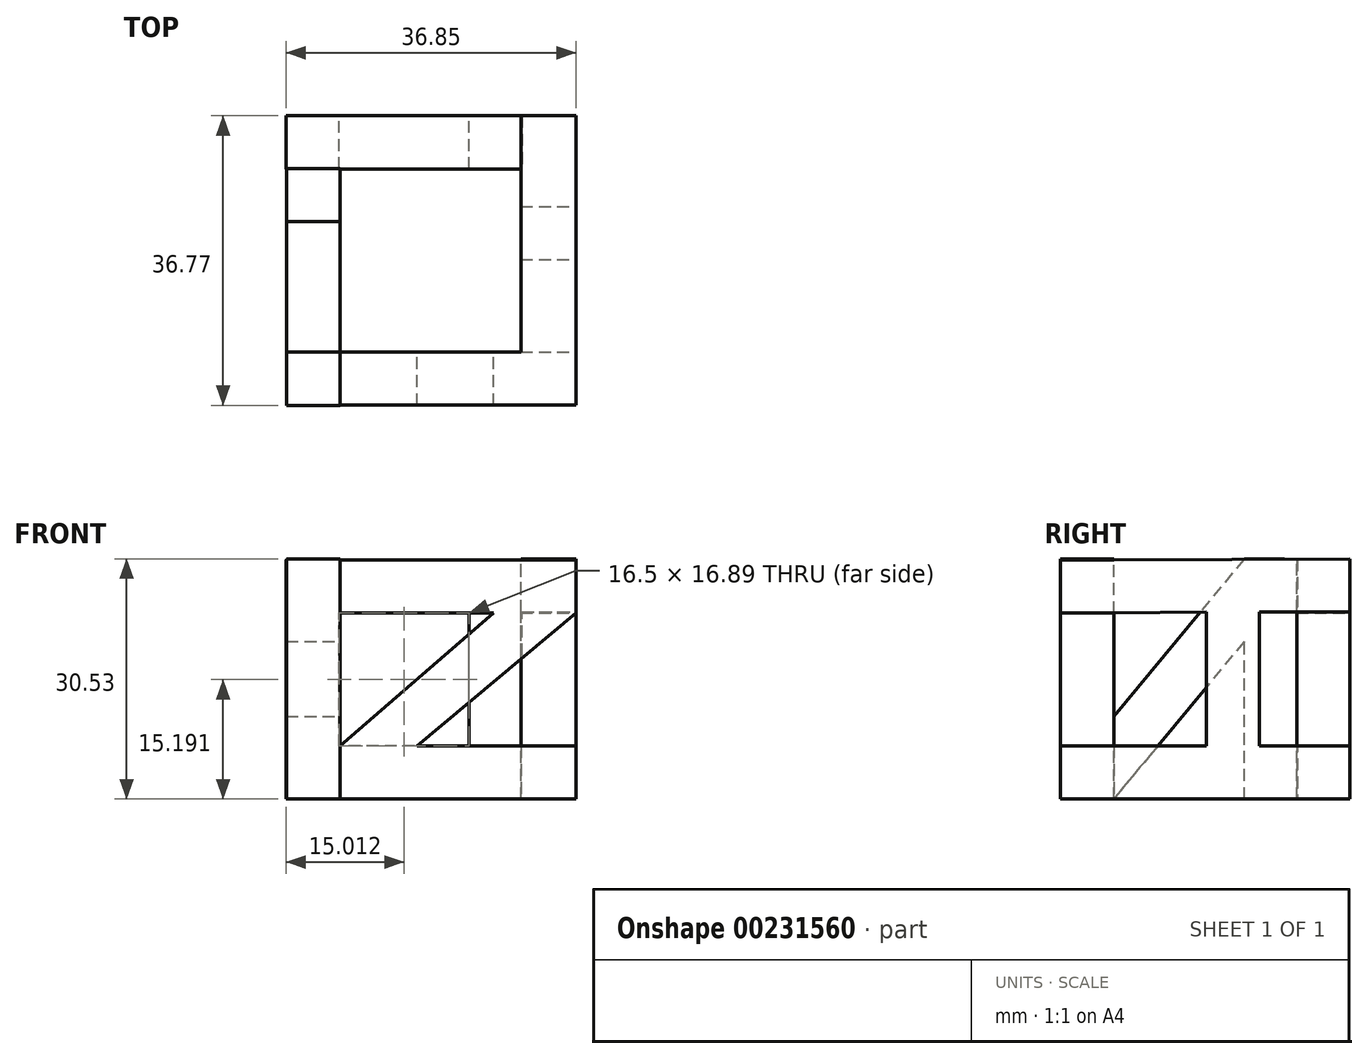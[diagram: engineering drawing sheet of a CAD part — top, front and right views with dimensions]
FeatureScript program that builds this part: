
annotation { "Feature Type Name" : "Feature", "Feature Type Description" : "" }
export const myFeature = defineFeature(function(context is Context, id is Id, definition is map)
    precondition{}
    {
        {
            var Q0;
            Q0=qCreatedBy(makeId("Front.planeOp"),FACE);
            cPlane(context, id + "F0", {"entities" : qUnion([Q0]), "cplaneType" : CPlaneType.OFFSET, "offset" : 30 * mm, "oppositeDirection" : true, "width" : 150 * mm, "height" : 150 * mm});
        }
        {
            var Q0;
            Q0=qCreatedBy(makeId("Front.planeOp"),FACE);
            var sketch = newSketch(context, id + "F1", { "sketchPlane" : qUnion([Q0])});
            skLineSegment(sketch, "E0", {"start": v(-30, -0.01) * mm, "end": v(0, -0.01) * mm});
            skLineSegment(sketch, "E1", {"start": v(0, 30.38) * mm, "end": v(-30, 30.38) * mm});
            skLineSegment(sketch, "E2", {"start": v(-30, 30.38) * mm, "end": v(-30, 23.62) * mm});
            skLineSegment(sketch, "E3", {"start": v(-30, 23.62) * mm, "end": v(-10.5, 23.62) * mm});
            skLineSegment(sketch, "E4", {"start": v(0, 23.62) * mm, "end": v(0, 30.38) * mm});
            skLineSegment(sketch, "E5", {"start": v(-30, -0.01) * mm, "end": v(-30, 6.74) * mm});
            skLineSegment(sketch, "E6", {"start": v(0, 6.74) * mm, "end": v(0, -0.01) * mm});
            skLineSegment(sketch, "E7.trimOffspring", {"start": v(-20.2, 6.74) * mm, "end": v(0, 6.74) * mm});
            skLineSegment(sketch, "E8", {"start": v(-20.2, 6.74) * mm, "end": v(0, 23.62) * mm});
            skLineSegment(sketch, "E9", {"start": v(-30, 6.74) * mm, "end": v(-10.5, 23.62) * mm});
            skSolve(sketch);
        }
        {
            var Q0;
            Q0=qCreatedBy(makeId("Right.planeOp"),FACE);
            var sketch = newSketch(context, id + "F2", { "sketchPlane" : qUnion([Q0])});
            skLineSegment(sketch, "E10", {"start": v(30, 23.77) * mm, "end": v(30, 30.52) * mm});
            skLineSegment(sketch, "E11", {"start": v(11.75, 6.75) * mm, "end": v(11.75, 23.77) * mm});
            skLineSegment(sketch, "E12", {"start": v(18.5, 6.75) * mm, "end": v(18.5, 23.77) * mm});
            skLineSegment(sketch, "E13.trimOffspring", {"start": v(18.5, 23.77) * mm, "end": v(30, 23.77) * mm});
            skLineSegment(sketch, "E14", {"start": v(30, 0) * mm, "end": v(30, 6.75) * mm});
            skLineSegment(sketch, "E15", {"start": v(30, 6.75) * mm, "end": v(18.5, 6.75) * mm});
            skLineSegment(sketch, "E16", {"start": v(0, 6.75) * mm, "end": v(0, 0) * mm});
            skLineSegment(sketch, "E17.trimOffspring", {"start": v(11.75, 6.75) * mm, "end": v(0, 6.75) * mm});
            skLineSegment(sketch, "E18", {"start": v(0, 0) * mm, "end": v(30, 0) * mm});
            skLineSegment(sketch, "E19", {"start": v(0, 30.38) * mm, "end": v(30, 30.52) * mm});
            skLineSegment(sketch, "E20", {"start": v(0, 23.62) * mm, "end": v(0, 30.38) * mm});
            skLineSegment(sketch, "E21", {"start": v(0, 23.62) * mm, "end": v(11.75, 23.77) * mm});
            skSolve(sketch);
        }
        {
            var Q0;
            Q0=qCreatedBy(id+"F0.planeOp",FACE);
            var sketch = newSketch(context, id + "F3", { "sketchPlane" : qUnion([Q0])});
            skLineSegment(sketch, "E22", {"start": v(-6.84, -0.01) * mm, "end": v(-36.84, -0.01) * mm});
            skLineSegment(sketch, "E23", {"start": v(-13.59, 6.74) * mm, "end": v(-30.09, 6.74) * mm});
            skLineSegment(sketch, "E24", {"start": v(-6.84, -0.01) * mm, "end": v(-6.84, 30.38) * mm});
            skLineSegment(sketch, "E25", {"start": v(-6.84, 30.38) * mm, "end": v(-36.85, 30.38) * mm});
            skLineSegment(sketch, "E26", {"start": v(-36.85, 30.38) * mm, "end": v(-36.84, -0.01) * mm});
            skLineSegment(sketch, "E27", {"start": v(-13.59, 6.74) * mm, "end": v(-13.59, 23.62) * mm});
            skLineSegment(sketch, "E28", {"start": v(-13.59, 23.62) * mm, "end": v(-30.09, 23.62) * mm});
            skLineSegment(sketch, "E29", {"start": v(-30.09, 6.74) * mm, "end": v(-30.09, 23.62) * mm});
            skSolve(sketch);
        }
        {
            var Q0;
            Q0 = qSketchRegion(id + "F1", true);
            extrude(context, id + "F4", {"entities" : qUnion([Q0]), "depth" : 6.75 * mm});
        }
        {
            var Q0;
            Q0 = qSketchRegion(id + "F3", true);
            extrude(context, id + "F5", {"entities" : qUnion([Q0]), "operationType" : NewBodyOperationType.ADD, "depth" : 6.75 * mm});
        }
        {
            var Q0;
            Q0=makeQuery(id+"F2.imprint","IMPRINT",FACE,{"disambiguationData":[TD([[makeQuery(id+"F2.imprint","IMPRINT",EDGE,{"derivedFrom":sQuery(id+"F2.wireOp",EDGE,"E10")}),1.0]])]});
            extrude(context, id + "F6", {"entities" : qUnion([Q0]), "operationType" : NewBodyOperationType.ADD, "oppositeDirection" : true, "depth" : 7 * mm});
        }
        {
            var Q0;
            Q0=qCreatedBy(makeId("Right.planeOp"),FACE);
            cPlane(context, id + "F7", {"entities" : qUnion([Q0]), "cplaneType" : CPlaneType.OFFSET, "offset" : 30 * mm, "oppositeDirection" : true, "width" : 150 * mm, "height" : 150 * mm});
        }
        {
            var Q0;
            Q0=qCreatedBy(id+"F7.planeOp",FACE);
            var sketch = newSketch(context, id + "F8", { "sketchPlane" : qUnion([Q0])});
            skLineSegment(sketch, "E30", {"start": v(23.33, -0.01) * mm, "end": v(16.58, -0.01) * mm});
            skLineSegment(sketch, "E31", {"start": v(-6.77, -0.01) * mm, "end": v(-6.77, 30.48) * mm});
            skLineSegment(sketch, "E32", {"start": v(-6.77, 30.48) * mm, "end": v(0, 30.48) * mm});
            skLineSegment(sketch, "E33", {"start": v(23.33, 30.48) * mm, "end": v(23.33, -0.01) * mm});
            skLineSegment(sketch, "E34", {"start": v(0, 30.48) * mm, "end": v(-6.77, 30.48) * mm});
            skLineSegment(sketch, "E35", {"start": v(16.58, -0.01) * mm, "end": v(16.58, 20) * mm});
            skLineSegment(sketch, "E36", {"start": v(16.58, 20) * mm, "end": v(0, 0) * mm});
            skLineSegment(sketch, "E37", {"start": v(16.58, 30.48) * mm, "end": v(0, 10.5) * mm});
            skLineSegment(sketch, "E38.trimOffspring", {"start": v(16.58, 30.48) * mm, "end": v(23.33, 30.48) * mm});
            skLineSegment(sketch, "E39", {"start": v(0, 10.5) * mm, "end": v(0, 30.48) * mm});
            skLineSegment(sketch, "E40", {"start": v(0, 0) * mm, "end": v(-6.77, -0.01) * mm});
            skSolve(sketch);
        }
        {
            var Q0;
            Q0 = qSketchRegion(id + "F8", true);
            extrude(context, id + "F9", {"entities" : qUnion([Q0]), "oppositeDirection" : true, "depth" : 6.8 * mm});
        }
    });
